# Revit family: 4. Секция моноблока UTR A
name_source: partatom
category: Оборудование
revit_build: Autodesk Revit 2016 (Build: 20151209_0715(x64)
units: mm (PartAtom-declared; Revit-internal decimal feet)

## family parameters
Всегда вертикально = Да
На основе рабочей плоскости = Нет
Общий = Нет
При загрузке вырезать с полостями = Нет
Размер круглого соединителя = Использовать диаметр
Тип детали = Нормальный
Точка расчета площади = Нет

## types (46) — shared parameters
h = 60 мм
Единица измерения = шт.
Завод изготовитель = KORF
Ключевая пометка = Вентиляция
Наименование и тех.хар-ка = Секция фильтра, водяного нагревателя и вентилятора
Раздел = ОВ
Синий = Синий
высота ножек = 50 мм
значок = Да

## per-type parameters (varying)
| type | А | А1 | Б | Б1 | Г | Д | Д1 | Масса единицы | Материал | Мощность двигателя N,Вт | Напряжение U,В | Сила тока J, А | Теплопроизводительность, кВт | Тип, марка, обозначение | Частота вращения n, об/мин | высота | размер В | ширина |
| 50-25 A.2.22-0,37x27(R) | 710 мм | 690 мм | 470 мм | 450 мм | 395 мм | 960 мм | 940 мм | 69 | RAL 0000 Серый металл | 370 | 3х220/3х380 | 1,66/0,96 | 26 кВт | UTR 50-25 A.2.22-0,37x27(R) | 2730 | 250 мм | 635 мм | 500 мм |
| 50-25 A.2.25-0,55x27(R) | 710 мм | 690 мм | 470 мм | 450 мм | 395 мм | 960 мм | 940 мм | 71 | Сталь серая | 550 | 3х220/3х380 | 2,47/1,43 | 26 кВт | UTR 50-25 A.2.22-0,55x27(R) | 2730 | 250 мм | 635 мм | 500 мм |
| 50-30 A.2.25-0,55x27(R) | 710 мм | 690 мм | 520 мм | 500 мм | 445 мм | 960 мм | 940 мм | 75 | Сталь серая | 550 | 3х220/3х380 | 2,47/1,43 | 30.9 кВт | UTR 50-30 A.2.25-0,55x27(R) | 2730 | 300 мм | 635 мм | 500 мм |
| 50-30 A.2.28-1,1x28(R) | 710 мм | 690 мм | 520 мм | 500 мм | 445 мм | 1060 мм | 1040 мм | 81 | Сталь серая | 1100 | 3х220/3х380 | 4,4/2,52 | 30.9 кВт | UTR 50-30 A.2.28-1,1x28(R) | 2800 | 300 мм | 635 мм | 500 мм |
| 50-30 A.2.31-1,1x28(R) | 710 мм | 690 мм | 520 мм | 500 мм | 445 мм | 1060 мм | 1040 мм | 83 | Сталь серая | 1100 | 3х220/3х380 | 4,4/2,52 | 30.9 кВт | UTR 50-30 A.2.31-1,1x28(R) | 2800 | 300 мм | 635 мм | 500 мм |
| 60-30 A.2.28-1,1x28(R) | 810 мм | 790 мм | 520 мм | 500 мм | 445 мм | 1060 мм | 1040 мм | 87 | Сталь серая | 1100 | 3х220/3х380 | 4,4/2,52 | 37.4 кВт | UTR 60-30 A.2.28-1,1x28(R) | 2800 | 300 мм | 735 мм | 600 мм |
| 60-30 A.2.31-1,1x28(R) | 810 мм | 790 мм | 520 мм | 500 мм | 445 мм | 1060 мм | 1040 мм | 89 | Сталь серая | 1100 | 3х220/3х380 | 4,4/2,52 | 37.4 кВт | UTR 60-30 A.2.31-1,1x28(R) | 2800 | 300 мм | 735 мм | 600 мм |
| 60-35 A.2.31-1,1x28(R) | 810 мм | 790 мм | 570 мм | 550 мм | 495 мм | 1060 мм | 1040 мм | 92 | Сталь серая | 1100 | 3х220/3х380 | 4,4/2,52 | 43.9 кВт | UTR 60-35 A.2.31-1,1x28(R) | 2800 | 350 мм | 735 мм | 600 мм |
| 60-35 A.2.31-1,5x28(R) | 810 мм | 790 мм | 570 мм | 550 мм | 495 мм | 1060 мм | 1040 мм | 95 | Сталь серая | 1500 | 3х220/3х380 | 5,6/3,3 | 43.9 кВт | UTR 60-35 A.2.31-1,5x28(R) | 2880 | 350 мм | 735 мм | 600 мм |
| 60-35 A.2.35-2,2x28(R) | 810 мм | 790 мм | 570 мм | 550 мм | 495 мм | 1140 мм | 1120 мм | 101 | Сталь серая | 1500 | 3х220/3х380 | 8,0/4,6 | 43.9 кВт | UTR 60-35 A.2.35-2,2x28(R) | 2860 | 350 мм | 735 мм | 600 мм |
| 70-40 A.2.31-1,1x28(R) | 910 мм | 890 мм | 620 мм | 600 мм | 545 мм | 1060 мм | 1040 мм | 102 | Сталь серая | 1100 | 3х220/3х380 | 4,4/2,52 | 58.5 кВт | UTR 70-40 A.2.31-1,1x28(R) | 2800 | 400 мм | 835 мм | 700 мм |
| 70-40 A.2.31-2,2x28(R) | 910 мм | 890 мм | 620 мм | 600 мм | 545 мм | 1140 мм | 1120 мм | 110 | Сталь серая | 2200 | 3х220/3х380 | 8,0/4,6 | 58.5 кВт | UTR 70-40 A.2.31-2,2x28(R) | 2860 | 400 мм | 835 мм | 700 мм |
| 70-40 A.2.35-2,2x28(R) | 910 мм | 890 мм | 620 мм | 600 мм | 545 мм | 1140 мм | 1120 мм | 111 | Сталь серая | 2200 | 3х220/3х380 | 8,0/4,6 | 58.5 кВт | UTR 70-40 A.2.35-2,2x28(R) | 2860 | 400 мм | 835 мм | 700 мм |
| 80-50 A.2.35-2,2x28(R) | 1010 мм | 990 мм | 720 мм | 700 мм | 645 мм | 1140 мм | 1120 мм | 126 | Сталь серая | 2200 | 3х220/3х380 | 8,0/4,6 | 82.9 кВт | UTR 80-50 A.2.35-2,2x28(R) | 2860 | 500 мм | 935 мм | 800 мм |
| 80-50 A.2.35-3,0x28(R) | 1010 мм | 990 мм | 720 мм | 700 мм | 645 мм | 1140 мм | 1120 мм | 130 | Сталь серая | 3000 | 3х220/3х380 | 10,5/6,0 | 82.9 кВт | UTR 80-50 A.2.35-3,0x28(R) | 2860 | 500 мм | 935 мм | 800 мм |
| 80-50 A.2.40-4,0x28(R) | 1010 мм | 990 мм | 720 мм | 700 мм | 645 мм | 1260 мм | 1240 мм | 147 | Сталь серая | 4000 | 3х380/3х660 | 8,0/4,6 | 82.9 кВт | UTR 80-50 A.2.40-4,0x28(R) | 2850 | 500 мм | 935 мм | 800 мм |
| 90-50 A.2.35-3,0x28(R) | 1160 мм | 1140 мм | 740 мм | 720 мм | 645 мм | 1140 мм | 1120 мм | 142 | Сталь серая | 3000 | 3х220/3х380 | 10,5/6,0 | 92.6 кВт | UTR 90-50 A.2.35-3,0x28(R) | 2860 | 500 мм | 1050 мм | 900 мм |
| 90-50 A.2.40-4,0x28(R) | 1160 мм | 1140 мм | 740 мм | 720 мм | 645 мм | 1260 мм | 1240 мм | 158 | Сталь серая | 4000 | 3х380/3х660 | 8,0/4,6 | 92.6 кВт | UTR 90-50 A.2.40-4,0x28(R) | 2850 | 500 мм | 1050 мм | 900 мм |
| 90-50 A.2.45-3,0x14(R) | 1160 мм | 1140 мм | 740 мм | 720 мм | 645 мм | 1260 мм | 1240 мм | 157 | Сталь серая | 3000 | 3х220/3х380 | 11,6/6,7 | 92.6 кВт | UTR 90-50 A.2.45-3,0x14(R) | 1410 | 500 мм | 1050 мм | 900 мм |
| 100-50 A.2.40-4,0x28(R) | 1225 мм | 1205 мм | 740 мм | 720 мм | 665 мм | 1260 мм | 1240 мм | 165 | Сталь серая | 4000 | 3х380/3х660 | 8,0/4,6 | 102.4 кВт | UTR 100-50 A.2.40-4,0x28(R) | 2850 | 500 мм | 1150 мм | 1000 мм |
| 100-50 A.2.45-3,0x28(R) | 1225 мм | 1205 мм | 740 мм | 720 мм | 665 мм | 1260 мм | 1240 мм | 166 | Сталь серая | 3000 | 3х220/3х380 | 11,6/6,7 | 102.4 кВт | UTR 100-50 A.2.45-3,0x14(R) | 1410 | 500 мм | 1150 мм | 1000 мм |
| 100-50 A.2.45-4,0x14(R) | 1225 мм | 1205 мм | 740 мм | 720 мм | 665 мм | 1320 мм | 1300 мм | 174 | Сталь серая | 4000 | 3х380/3х660 | 8,5/4,9 | 102.4 кВт | UTR 100-50 A.2.45-4,0x14(R) | 1410 | 500 мм | 1150 мм | 1000 мм |
| 100-50 A.2.45-5,5x14(R) | 1225 мм | 1205 мм | 740 мм | 720 мм | 665 мм | 1320 мм | 1300 мм | 183 | Сталь серая | 5500 | 3х380/3х660 | 11,0/6,5 | 102.4 кВт | UTR 100-50 A.2.45-5,5x14(R) | 1430 | 500 мм | 1150 мм | 1000 мм |
| 50-25 A.3.22-0,37x27(R) | 710 мм | 690 мм | 470 мм | 450 мм | 395 мм | 960 мм | 940 мм | 71 | Сталь серая | 370 | 3х220/3х380 | 1,66/0,96 | 31.4 кВт | UTR 50-25 A.3.22-0,37x27(R) | 2730 | 250 мм | 635 мм | 500 мм |
| 50-25 A.3.22-0,55x27(R) | 710 мм | 690 мм | 470 мм | 450 мм | 395 мм | 960 мм | 940 мм | 73 | Сталь серая | 550 | 3х220/3х380 | 2,47/1,43 | 31.4 кВт | UTR 50-25 A.3.22-0,55x27(R) | 2730 | 250 мм | 635 мм | 500 мм |
| 50-30 A.3.25-0,55x27(R) | 710 мм | 690 мм | 520 мм | 500 мм | 445 мм | 960 мм | 940 мм | 76 | Сталь серая | 550 | 3х220/3х380 | 2,47/1,43 | 37.3 кВт | UTR 50-30 A.3.25-0,55x27(R) | 2730 | 300 мм | 635 мм | 500 мм |
| 50-30 A.3.28-1,1x28(R) | 710 мм | 690 мм | 520 мм | 500 мм | 445 мм | 1060 мм | 1040 мм | 82 | Сталь серая | 1100 | 3х220/3х380 | 4,4/2,52 | 37.3 кВт | UTR 50-30 A.3.28-1,1x28(R) | 2800 | 300 мм | 635 мм | 500 мм |
| 50-30 A.3.31-1,1x28(R) | 710 мм | 690 мм | 520 мм | 500 мм | 445 мм | 1060 мм | 1040 мм | 84 | Сталь серая | 1100 | 3х220/3х380 | 4,4/2,52 | 37.3 кВт | UTR 50-30 A.3.31-1,1x28(R) | 2800 | 300 мм | 635 мм | 500 мм |
| 60-30 A.3.28-1,1x28(R) | 810 мм | 790 мм | 520 мм | 500 мм | 445 мм | 1060 мм | 1040 мм | 89 | Сталь серая | 1100 | 3х220/3х380 | 4,4/2,52 | 45.2 кВт | UTR 60-30 A.3.28-1,1x28(R) | 2800 | 300 мм | 735 мм | 600 мм |
| 60-30 A.3.31-1,1x28(R) | 810 мм | 790 мм | 520 мм | 500 мм | 445 мм | 1060 мм | 1040 мм | 91 | Сталь серая | 1100 | 3х220/3х380 | 4,4/2,52 | 45.2 кВт | UTR 60-30 A.3.31-1,1x28(R) | 2800 | 300 мм | 735 мм | 600 мм |
| 60-35 A.3.31-1,1x28(R) | 810 мм | 790 мм | 570 мм | 550 мм | 495 мм | 1060 мм | 1040 мм | 94 | Сталь серая | 1100 | 3х220/3х380 | 4,4/2,52 | 53 кВт | UTR 60-35 A.3.31-1,1x28(R) | 2800 | 350 мм | 735 мм | 600 мм |
| 60-35 A.3.31-1,5x28(R) | 810 мм | 790 мм | 570 мм | 550 мм | 495 мм | 1060 мм | 1040 мм | 97 | Сталь серая | 1500 | 3х220/3х380 | 5,6/3,3 | 53 кВт | UTR 60-35 A.3.31-1,5x28(R) | 2880 | 350 мм | 735 мм | 600 мм |
| 60-35 A.3.35-2,2x28(R) | 810 мм | 790 мм | 570 мм | 550 мм | 495 мм | 1140 мм | 1120 мм | 103 | Сталь серая | 1500 | 3х220/3х380 | 8,0/4,6 | 53 кВт | UTR 60-35 A.3.35-2,2x28(R) | 2860 | 350 мм | 735 мм | 600 мм |
| 70-40 A.3.31-1,1x28(R) | 910 мм | 890 мм | 620 мм | 600 мм | 545 мм | 1060 мм | 1040 мм | 105 | Сталь серая | 1100 | 3х220/3х380 | 4,4/2,52 | 70.7 кВт | UTR 70-40 A.3.31-1,1x28(R) | 2800 | 400 мм | 835 мм | 700 мм |
| 70-40 A.3.31-2,2x28(R) | 910 мм | 890 мм | 620 мм | 600 мм | 545 мм | 1140 мм | 1120 мм | 113 | Сталь серая | 2200 | 3х220/3х380 | 8,0/4,6 | 70.7 кВт | UTR 70-40 A.3.31-2,2x28(R) | 2860 | 400 мм | 835 мм | 700 мм |
| 70-40 A.3.35-2,2x28(R) | 910 мм | 890 мм | 620 мм | 600 мм | 545 мм | 1140 мм | 1120 мм | 114 | Сталь серая | 2200 | 3х220/3х380 | 8,0/4,6 | 70.7 кВт | UTR 70-40 A.3.35-2,2x28(R) | 2860 | 400 мм | 835 мм | 700 мм |
| 80-50 A.3.35-2,2x28(R) | 1010 мм | 990 мм | 720 мм | 700 мм | 645 мм | 1140 мм | 1120 мм | 129 | Сталь серая | 2200 | 3х220/3х380 | 8,0/4,6 | 100.1 кВт | UTR 80-50 A.3.35-2,2x28(R) | 2860 | 500 мм | 935 мм | 800 мм |
| 80-50 A.3.35-3,0x28(R) | 1010 мм | 990 мм | 720 мм | 700 мм | 645 мм | 1140 мм | 1120 мм | 133 | Сталь серая | 3000 | 3х220/3х380 | 10,5/6,0 | 100.1 кВт | UTR 80-50 A.3.35-3,0x28(R) | 2860 | 500 мм | 935 мм | 800 мм |
| 80-50 A.3.40-4,0x28(R) | 1010 мм | 990 мм | 720 мм | 700 мм | 645 мм | 1260 мм | 1240 мм | 150 | Сталь серая | 4000 | 3х380/3х660 | 8,0/4,6 | 100.1 кВт | UTR 80-50 A.3.40-4,0x28(R) | 2850 | 500 мм | 935 мм | 800 мм |
| 90-50 A.3.35-3,0x28(R) | 1160 мм | 1140 мм | 740 мм | 720 мм | 645 мм | 1140 мм | 1120 мм | 147 | Сталь серая | 3000 | 3х220/3х380 | 10,5/6,0 | 111.9 кВт | UTR 90-50 A.3.35-3,0x28(R) | 2860 | 500 мм | 1050 мм | 900 мм |
| 90-50 A.3.40-4,0x28(R) | 1160 мм | 1140 мм | 740 мм | 720 мм | 645 мм | 1260 мм | 1240 мм | 161 | Сталь серая | 4000 | 3х380/3х660 | 8,0/4,6 | 111.9 кВт | UTR 90-50 A.3.40-4,0x28(R) | 2850 | 500 мм | 1050 мм | 900 мм |
| 90-50 A.3.45-3,0x14(R) | 1160 мм | 1140 мм | 740 мм | 720 мм | 645 мм | 1260 мм | 1240 мм | 162 | Сталь серая | 3000 | 3х220/3х380 | 11,6/6,7 | 111.9 кВт | UTR 90-50 A.3.45-3,0x14(R) | 1410 | 500 мм | 1050 мм | 900 мм |
| 100-50 A.3.40-4,0x28(R) | 1225 мм | 1205 мм | 740 мм | 720 мм | 665 мм | 1260 мм | 1240 мм | 170 | Сталь серая | 4000 | 3х380/3х660 | 8,0/4,6 | 123.7 кВт | UTR 100-50 A.3.40-4,0x28(R) | 2850 | 500 мм | 1150 мм | 1000 мм |
| 100-50 A.3.45-3,0x14(R) | 1225 мм | 1205 мм | 740 мм | 720 мм | 665 мм | 1260 мм | 1240 мм | 169 | Сталь серая | 3000 | 3х220/3х380 | 11,6/6,7 | 123.7 кВт | UTR 100-50 A.3.45-3,0x14(R) | 1410 | 500 мм | 1150 мм | 1000 мм |
| 100-50 A.3.45-4,0x14(R) | 1225 мм | 1205 мм | 740 мм | 720 мм | 665 мм | 1320 мм | 1300 мм | 179 | Сталь серая | 4000 | 3х380/3х660 | 8,5/4,9 | 123.7 кВт | UTR 100-50 A.3.45-4,0x14(R) | 1410 | 500 мм | 1150 мм | 1000 мм |
| 100-50 A.3.45-5,5x14(R) | 1225 мм | 1205 мм | 740 мм | 720 мм | 665 мм | 1320 мм | 1300 мм | 188 | Сталь серая | 5500 | 3х380/3х660 | 11,0/6,5 | 123.7 кВт | UTR 100-50 A.3.45-5,5x14(R) | 1430 | 500 мм | 1150 мм | 1000 мм |
